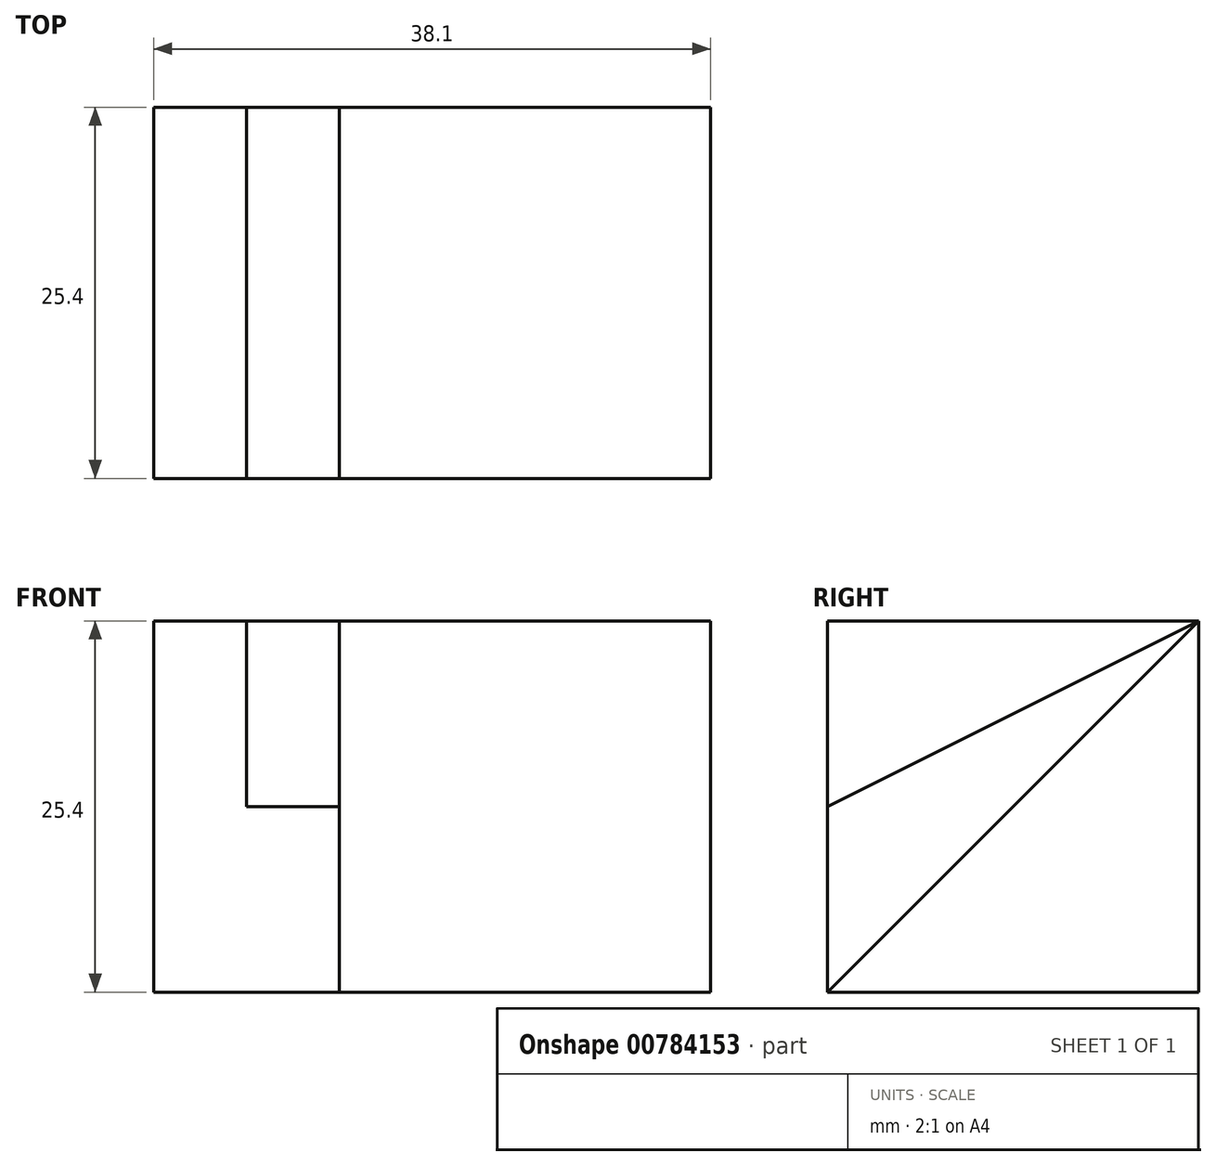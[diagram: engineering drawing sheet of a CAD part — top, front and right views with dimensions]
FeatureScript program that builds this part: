
annotation { "Feature Type Name" : "Feature", "Feature Type Description" : "" }
export const myFeature = defineFeature(function(context is Context, id is Id, definition is map)
    precondition{}
    {
        {
            var Q0;
            Q0=qCreatedBy(makeId("Right.planeOp"),FACE);
            var sketch = newSketch(context, id + "F0", { "sketchPlane" : qUnion([Q0])});
            skLineSegment(sketch, "E0", {"start": v(0, 0) * mm, "end": v(0, 25.4) * mm});
            skLineSegment(sketch, "E1", {"start": v(0, 25.4) * mm, "end": v(25.4, 25.4) * mm});
            skLineSegment(sketch, "E2", {"start": v(25.4, 25.4) * mm, "end": v(25.4, 0) * mm});
            skLineSegment(sketch, "E3", {"start": v(25.4, 0) * mm, "end": v(0, 0) * mm});
            skLineSegment(sketch, "E4", {"start": v(0, 12.7) * mm, "end": v(25.4, 25.4) * mm});
            skLineSegment(sketch, "E5", {"start": v(0, 25.4) * mm, "end": v(0, 19.05) * mm});
            skPoint(sketch, "E5.endSnap0", {"position": v(12.7, 19.05) * mm});
            skLineSegment(sketch, "E6", {"start": v(0, 0) * mm, "end": v(25.4, 25.4) * mm});
            skSolve(sketch);
        }
        {
            var Q0;
            Q0=makeQuery(id+"F0.imprint","IMPRINT",FACE,{"disambiguationData":[TD([[makeQuery(id+"F0.imprint","IMPRINT",EDGE,{"derivedFrom":sQuery(id+"F0.wireOp",EDGE,"E2")}),-1.0]])]});
            extrude(context, id + "F1", {"entities" : qUnion([Q0]), "depth" : 38.1 * mm, "offsetDistance" : 25.4 * mm});
        }
        {
            var Q0;
            {var subQ2=sQuery(id+"F0.wireOp",EDGE,"E4");Q0=makeQuery(id+"F0.imprint","IMPRINT",FACE,{"disambiguationData":[TD([[makeQuery(id+"F0.imprint","IMPRINT",EDGE,{"derivedFrom":subQ2}),-1.0]])]});}
            extrude(context, id + "F2", {"entities" : qUnion([Q0]), "operationType" : NewBodyOperationType.ADD, "depth" : 12.7 * mm, "offsetDistance" : 25.4 * mm});
        }
        {
            var Q0;
            Q0=makeQuery(id+"F0.imprint","IMPRINT",FACE,{"disambiguationData":[TD([[makeQuery(id+"F0.imprint","IMPRINT",EDGE,{"derivedFrom":sQuery(id+"F0.wireOp",EDGE,"E1")}),-1.0]])]});
            extrude(context, id + "F3", {"entities" : qUnion([Q0]), "operationType" : NewBodyOperationType.ADD, "depth" : 6.35 * mm, "offsetDistance" : 25.4 * mm});
        }
    });
